FCSTD DOCUMENT  (FreeCAD 0.20R29410 (Git))
Label: parallel_port_pinout
License: All rights reserved
LicenseURL: http://en.wikipedia.org/wiki/All_rights_reserved
objects: App::FeaturePython×43, Part::Part2DObjectPython×25, Sketcher::SketchObject×1, Part::Feature×1, App::DocumentObjectGroup×1, TechDraw::DrawSVGTemplate×1, App::Part×1, TechDraw::DrawViewPart×1, TechDraw::DrawPage×1
note: 27 computed .brp shape members not serialized (recipe doc carries the construction recipe); baked Part::Feature solids carry a one-line shape summary decoded from their .brp

FEATURE [Sketcher::SketchObject] Sketch
  FullyConstrained = false
  sketch-geometry (45):
    g0: Circle CenterX=-16.62 CenterY=1.42 CenterZ=0 NormalX=0 NormalY=0 NormalZ=1 AngleXU=0 Radius=0.64
    g1: Circle CenterX=-13.85 CenterY=1.42 CenterZ=0 NormalX=0 NormalY=0 NormalZ=1 AngleXU=0 Radius=0.64
    g2: Circle CenterX=-11.08 CenterY=1.42 CenterZ=0 NormalX=0 NormalY=0 NormalZ=1 AngleXU=0 Radius=0.64
    g3: Circle CenterX=-8.31 CenterY=1.42 CenterZ=0 NormalX=0 NormalY=0 NormalZ=1 AngleXU=0 Radius=0.64
    g4: Circle CenterX=16.62 CenterY=1.42 CenterZ=0 NormalX=0 NormalY=0 NormalZ=1 AngleXU=0 Radius=0.64
    g5: LineSegment StartX=-16.62 StartY=1.42 StartZ=0 EndX=16.62 EndY=1.42 EndZ=0
    g6: Circle CenterX=-5.54 CenterY=1.42 CenterZ=0 NormalX=0 NormalY=0 NormalZ=1 AngleXU=0 Radius=0.64
    g7: Circle CenterX=-2.77 CenterY=1.42 CenterZ=0 NormalX=0 NormalY=0 NormalZ=1 AngleXU=0 Radius=0.64
    g8: Circle CenterX=-2e-16 CenterY=1.42 CenterZ=0 NormalX=0 NormalY=0 NormalZ=1 AngleXU=0 Radius=0.64
    g9: Circle CenterX=2.77 CenterY=1.42 CenterZ=0 NormalX=0 NormalY=0 NormalZ=1 AngleXU=0 Radius=0.64
    g10: Circle CenterX=5.54 CenterY=1.42 CenterZ=0 NormalX=0 NormalY=0 NormalZ=1 AngleXU=0 Radius=0.64
    g11: Circle CenterX=8.31 CenterY=1.42 CenterZ=0 NormalX=0 NormalY=0 NormalZ=1 AngleXU=0 Radius=0.64
    g12: Circle CenterX=11.08 CenterY=1.42 CenterZ=0 NormalX=0 NormalY=0 NormalZ=1 AngleXU=0 Radius=0.64
    g13: Circle CenterX=13.85 CenterY=1.42 CenterZ=0 NormalX=0 NormalY=0 NormalZ=1 AngleXU=0 Radius=0.64
    g14: LineSegment StartX=-15.235 StartY=-1.42 StartZ=0 EndX=15.235 EndY=-1.42 EndZ=0
    g15: Circle CenterX=-15.235 CenterY=-1.42 CenterZ=0 NormalX=0 NormalY=0 NormalZ=1 AngleXU=0 Radius=0.64
    g16: Circle CenterX=-12.465 CenterY=-1.42 CenterZ=0 NormalX=0 NormalY=0 NormalZ=1 AngleXU=0 Radius=0.64
    g17: Circle CenterX=-9.695 CenterY=-1.42 CenterZ=0 NormalX=0 NormalY=0 NormalZ=1 AngleXU=0 Radius=0.64
    g18: Circle CenterX=-6.925 CenterY=-1.42 CenterZ=0 NormalX=0 NormalY=0 NormalZ=1 AngleXU=0 Radius=0.64
    g19: Circle CenterX=-4.155 CenterY=-1.42 CenterZ=0 NormalX=0 NormalY=0 NormalZ=1 AngleXU=0 Radius=0.64
    g20: Circle CenterX=-1.385 CenterY=-1.42 CenterZ=0 NormalX=0 NormalY=0 NormalZ=1 AngleXU=0 Radius=0.64
    g21: Circle CenterX=1.385 CenterY=-1.42 CenterZ=0 NormalX=0 NormalY=0 NormalZ=1 AngleXU=0 Radius=0.64
    g22: Circle CenterX=4.155 CenterY=-1.42 CenterZ=0 NormalX=0 NormalY=0 NormalZ=1 AngleXU=0 Radius=0.64
    g23: Circle CenterX=6.925 CenterY=-1.42 CenterZ=0 NormalX=0 NormalY=0 NormalZ=1 AngleXU=0 Radius=0.64
    g24: Circle CenterX=9.695 CenterY=-1.42 CenterZ=0 NormalX=0 NormalY=0 NormalZ=1 AngleXU=0 Radius=0.64
    g25: Circle CenterX=12.465 CenterY=-1.42 CenterZ=0 NormalX=0 NormalY=0 NormalZ=1 AngleXU=0 Radius=0.64
    g26: Circle CenterX=15.235 CenterY=-1.42 CenterZ=0 NormalX=0 NormalY=0 NormalZ=1 AngleXU=0 Radius=0.64
    g27: GeomPoint X=-2e-16 Y=-1.42 Z=0
    g28: LineSegment StartX=-16.81 StartY=4.18 StartZ=0 EndX=16.81 EndY=4.18 EndZ=0
    g29: LineSegment StartX=-16.2775 StartY=-4.18 StartZ=0 EndX=16.2775 EndY=-4.18 EndZ=0
    g30: LineSegment StartX=19.4394 StartY=1.04636 StartZ=0 EndX=18.9069 EndY=-1.97364 EndZ=0
    g31: LineSegment StartX=-19.4394 StartY=1.04636 StartZ=0 EndX=-18.9069 EndY=-1.97364 EndZ=0
    g32: ArcOfCircle CenterX=-16.81 CenterY=1.51 CenterZ=0 NormalX=0 NormalY=0 NormalZ=1 AngleXU=0 Radius=2.67 StartAngle=1.5708 EndAngle=3.31613
    g33: ArcOfCircle CenterX=-16.2775 CenterY=-1.51 CenterZ=0 NormalX=0 NormalY=0 NormalZ=1 AngleXU=0 Radius=2.67 StartAngle=3.31613 EndAngle=4.71239
    g34: ArcOfCircle CenterX=16.81 CenterY=1.51 CenterZ=0 NormalX=0 NormalY=0 NormalZ=1 AngleXU=0 Radius=2.67 StartAngle=6.10865 EndAngle=7.85398
    g35: ArcOfCircle CenterX=16.2775 CenterY=-1.51 CenterZ=0 NormalX=0 NormalY=0 NormalZ=1 AngleXU=0 Radius=2.67 StartAngle=4.71239 EndAngle=6.10865
    g36: LineSegment StartX=19.4394 StartY=1.04636 StartZ=0 EndX=19.4394 EndY=-2.3777 EndZ=0
    g37: LineSegment StartX=-19.4394 StartY=1.04636 StartZ=0 EndX=-19.4394 EndY=-0.673424 EndZ=0
    g38: LineSegment StartX=-16.81 StartY=1.51 StartZ=0 EndX=16.81 EndY=1.51 EndZ=0
    g39: LineSegment StartX=-16.2775 StartY=-1.51 StartZ=0 EndX=16.2775 EndY=-1.51 EndZ=0
    g40: LineSegment StartX=-19.48 StartY=3.07637 StartZ=0 EndX=-19.48 EndY=-2.31562 EndZ=0
    g41: GeomPoint X=-19.48 Y=1.50999 Z=0
    g42: LineSegment StartX=16.81 StartY=1.51 StartZ=0 EndX=19.48 EndY=1.51 EndZ=0
    g43: GeomPoint X=0 Y=4.18 Z=0
    g44: GeomPoint X=0 Y=-4.18 Z=0
  constraints (114):
    c: Coincident(g5,g0)
    c: Coincident(g5,g4)
    c: PointOnObject(g3,g5)
    c: PointOnObject(g2,g5)
    c: PointOnObject(g1,g5)
    c: PointOnObject(g6,g5)
    c: PointOnObject(g7,g5)
    c: PointOnObject(g8,g5)
    c: PointOnObject(g9,g5)
    c: PointOnObject(g10,g5)
    c: PointOnObject(g11,g5)
    c: PointOnObject(g12,g5)
    c: PointOnObject(g13,g5)
    c: Equal(g3,g2)
    c: Equal(g2,g1)
    c: Equal(g1,g0)
    c: Equal(g0,g6)
    c: Equal(g6,g7)
    c: Equal(g7,g8)
    c: Equal(g8,g9)
    c: Equal(g9,g10)
    c: Equal(g10,g11)
    c: Equal(g11,g12)
    c: Equal(g12,g13)
    c: Equal(g13,g4)
    c: Radius(g0) = 0.64
    c: DistanceX(g0,g1) = 2.77
    c: DistanceX(g1,g2) = 2.77
    c: DistanceX(g2,g3) = 2.77
    c: DistanceX(g3,g6) = 2.77
    c: DistanceX(g6,g7) = 2.77
    c: DistanceX(g7,g8) = 2.77
    c: DistanceX(g8,g9) = 2.77
    c: DistanceX(g9,g10) = 2.77
    c: DistanceX(g10,g11) = 2.77
    c: DistanceX(g11,g12) = 2.77
    c: DistanceX(g12,g13) = 2.77
    c: DistanceX(g13,g4) = 2.77
    c: Symmetric(g0,g4,g-2)
    c: Symmetric(g14,g14,g-2)
    c: Coincident(g15,g14)
    c: PointOnObject(g16,g14)
    c: PointOnObject(g17,g14)
    c: PointOnObject(g18,g14)
    c: PointOnObject(g19,g14)
    c: PointOnObject(g20,g14)
    c: PointOnObject(g21,g14)
    c: PointOnObject(g22,g14)
    c: PointOnObject(g23,g14)
    c: PointOnObject(g24,g14)
    c: PointOnObject(g25,g14)
    c: Coincident(g26,g14)
    c: Equal(g15,g16)
    c: Equal(g16,g17)
    c: Equal(g17,g18)
    c: Equal(g18,g19)
    c: Equal(g19,g20)
    c: Equal(g20,g21)
    c: Equal(g21,g22)
    c: Equal(g22,g23)
    c: Equal(g23,g24)
    c: Equal(g24,g25)
    c: Equal(g25,g26)
    c: Equal(g26,g0)
    c: DistanceX(g14,g16) = 2.77
    c: DistanceX(g16,g17) = 2.77
    c: DistanceX(g17,g18) = 2.77
    c: DistanceX(g18,g19) = 2.77
    c: DistanceX(g19,g20) = 2.77
    c: DistanceX(g20,g21) = 2.77
    c: DistanceX(g21,g22) = 2.77
    c: DistanceX(g22,g23) = 2.77
    c: DistanceX(g23,g24) = 2.77
    c: DistanceX(g24,g25) = 2.77
    c: DistanceX(g25,g14) = 2.77
    c: DistanceY(g15,g0) = 2.84
    c: PointOnObject(g27,g14)
    c: Symmetric(g27,g8,g-1)
    c: Tangent(g32,g31) = -1.5708
    c: Tangent(g28,g32) = 1.5708
    c: Tangent(g33,g31) = -1.5708
    c: Tangent(g33,g29) = -1.5708
    c: Tangent(g34,g28) = 1.5708
    c: Tangent(g34,g30) = 1.5708
    c: Tangent(g35,g29) = -1.5708
    c: Tangent(g35,g30) = 1.5708
    c: Coincident(g36,g30)
    c: Vertical(g36)
    c: Angle(g30,g36) = 0.174533
    c: Coincident(g37,g31)
    c: Vertical(g37)
    c: Angle(g37,g31) = 0.174533
    c: DistanceY(g29,g28) = 8.36
    c: Symmetric(g28,g28,g-2)
    c: Symmetric(g29,g29,g-2)
    c: Coincident(g38,g32)
    c: Coincident(g38,g34)
    c: Horizontal(g38)
    c: Coincident(g39,g33)
    c: Coincident(g39,g35)
    c: Vertical(g40)
    c: Tangent(g40,g32)
    c: PointOnObject(g41,g32)
    c: PointOnObject(g41,g40)
    c: Coincident(g42,g34)
    c: Horizontal(g42)
    c: PointOnObject(g42,g34)
    c: DistanceX(g41,g42) = 38.96
    c: PointOnObject(g43,g-2)
    c: PointOnObject(g43,g28)
    c: PointOnObject(g44,g29)
    c: Symmetric(g44,g43,g-1)
    c: Radius(g32) = 2.67
    c: Equal(g33,g32)
FEATURE [Part::Part2DObjectPython] Circle  # Draft 2D object (typed FeaturePython)
  Area = 1.2868
  FirstAngle = 0
  LastAngle = 0
  MakeFace = true
  Placement = pos=(-16.62,1.42,0) rot=(0,0,1;0rad)
  Radius = 0.64
FEATURE [Part::Part2DObjectPython] Circle001  # Draft 2D object (typed FeaturePython)
  Area = 1.2868
  FirstAngle = 0
  LastAngle = 0
  MakeFace = true
  Placement = pos=(-13.85,1.42,0) rot=(0,0,1;0rad)
  Radius = 0.64
FEATURE [Part::Part2DObjectPython] Circle002  # Draft 2D object (typed FeaturePython)
  Area = 1.2868
  FirstAngle = 0
  LastAngle = 0
  MakeFace = true
  Placement = pos=(-11.08,1.42,0) rot=(0,0,1;0rad)
  Radius = 0.64
FEATURE [Part::Part2DObjectPython] Circle003  # Draft 2D object (typed FeaturePython)
  Area = 1.2868
  FirstAngle = 0
  LastAngle = 0
  MakeFace = true
  Placement = pos=(-8.31,1.42,0) rot=(0,0,1;0rad)
  Radius = 0.64
FEATURE [Part::Part2DObjectPython] Circle004  # Draft 2D object (typed FeaturePython)
  Area = 1.2868
  FirstAngle = 0
  LastAngle = 0
  MakeFace = true
  Placement = pos=(16.62,1.42,0) rot=(0,0,1;0rad)
  Radius = 0.64
FEATURE [Part::Part2DObjectPython] Circle005  # Draft 2D object (typed FeaturePython)
  Area = 1.2868
  FirstAngle = 0
  LastAngle = 0
  MakeFace = true
  Placement = pos=(-5.54,1.42,0) rot=(0,0,1;0rad)
  Radius = 0.64
FEATURE [Part::Part2DObjectPython] Circle006  # Draft 2D object (typed FeaturePython)
  Area = 1.2868
  FirstAngle = 0
  LastAngle = 0
  MakeFace = true
  Placement = pos=(-2.77,1.42,0) rot=(0,0,1;0rad)
  Radius = 0.64
FEATURE [Part::Part2DObjectPython] Circle007  # Draft 2D object (typed FeaturePython)
  Area = 1.2868
  FirstAngle = 0
  LastAngle = 0
  MakeFace = true
  Placement = pos=(-2e-16,1.42,0) rot=(0,0,1;0rad)
  Radius = 0.64
FEATURE [Part::Part2DObjectPython] Circle008  # Draft 2D object (typed FeaturePython)
  Area = 1.2868
  FirstAngle = 0
  LastAngle = 0
  MakeFace = true
  Placement = pos=(2.77,1.42,0) rot=(0,0,1;0rad)
  Radius = 0.64
FEATURE [Part::Part2DObjectPython] Circle009  # Draft 2D object (typed FeaturePython)
  Area = 1.2868
  FirstAngle = 0
  LastAngle = 0
  MakeFace = true
  Placement = pos=(5.54,1.42,0) rot=(0,0,1;0rad)
  Radius = 0.64
FEATURE [Part::Part2DObjectPython] Circle010  # Draft 2D object (typed FeaturePython)
  Area = 1.2868
  FirstAngle = 0
  LastAngle = 0
  MakeFace = true
  Placement = pos=(8.31,1.42,0) rot=(0,0,1;0rad)
  Radius = 0.64
FEATURE [Part::Part2DObjectPython] Circle011  # Draft 2D object (typed FeaturePython)
  Area = 1.2868
  FirstAngle = 0
  LastAngle = 0
  MakeFace = true
  Placement = pos=(11.08,1.42,0) rot=(0,0,1;0rad)
  Radius = 0.64
FEATURE [Part::Part2DObjectPython] Circle012  # Draft 2D object (typed FeaturePython)
  Area = 1.2868
  FirstAngle = 0
  LastAngle = 0
  MakeFace = true
  Placement = pos=(13.85,1.42,0) rot=(0,0,1;0rad)
  Radius = 0.64
FEATURE [Part::Part2DObjectPython] Circle013  # Draft 2D object (typed FeaturePython)
  Area = 1.2868
  FirstAngle = 0
  LastAngle = 0
  MakeFace = true
  Placement = pos=(-15.235,-1.42,0) rot=(0,0,1;0rad)
  Radius = 0.64
FEATURE [Part::Part2DObjectPython] Circle014  # Draft 2D object (typed FeaturePython)
  Area = 1.2868
  FirstAngle = 0
  LastAngle = 0
  MakeFace = true
  Placement = pos=(-12.465,-1.42,0) rot=(0,0,1;0rad)
  Radius = 0.64
FEATURE [Part::Part2DObjectPython] Circle015  # Draft 2D object (typed FeaturePython)
  Area = 1.2868
  FirstAngle = 0
  LastAngle = 0
  MakeFace = true
  Placement = pos=(-9.695,-1.42,0) rot=(0,0,1;0rad)
  Radius = 0.64
FEATURE [Part::Part2DObjectPython] Circle016  # Draft 2D object (typed FeaturePython)
  Area = 1.2868
  FirstAngle = 0
  LastAngle = 0
  MakeFace = true
  Placement = pos=(-6.925,-1.42,0) rot=(0,0,1;0rad)
  Radius = 0.64
FEATURE [Part::Part2DObjectPython] Circle017  # Draft 2D object (typed FeaturePython)
  Area = 1.2868
  FirstAngle = 0
  LastAngle = 0
  MakeFace = true
  Placement = pos=(-4.155,-1.42,0) rot=(0,0,1;0rad)
  Radius = 0.64
FEATURE [Part::Part2DObjectPython] Circle018  # Draft 2D object (typed FeaturePython)
  Area = 1.2868
  FirstAngle = 0
  LastAngle = 0
  MakeFace = true
  Placement = pos=(-1.385,-1.42,0) rot=(0,0,1;0rad)
  Radius = 0.64
FEATURE [Part::Part2DObjectPython] Circle019  # Draft 2D object (typed FeaturePython)
  Area = 1.2868
  FirstAngle = 0
  LastAngle = 0
  MakeFace = true
  Placement = pos=(1.385,-1.42,0) rot=(0,0,1;0rad)
  Radius = 0.64
FEATURE [Part::Part2DObjectPython] Circle020  # Draft 2D object (typed FeaturePython)
  Area = 1.2868
  FirstAngle = 0
  LastAngle = 0
  MakeFace = true
  Placement = pos=(4.155,-1.42,0) rot=(0,0,1;0rad)
  Radius = 0.64
FEATURE [Part::Part2DObjectPython] Circle021  # Draft 2D object (typed FeaturePython)
  Area = 1.2868
  FirstAngle = 0
  LastAngle = 0
  MakeFace = true
  Placement = pos=(6.925,-1.42,0) rot=(0,0,1;0rad)
  Radius = 0.64
FEATURE [Part::Part2DObjectPython] Circle022  # Draft 2D object (typed FeaturePython)
  Area = 1.2868
  FirstAngle = 0
  LastAngle = 0
  MakeFace = true
  Placement = pos=(9.695,-1.42,0) rot=(0,0,1;0rad)
  Radius = 0.64
FEATURE [Part::Part2DObjectPython] Circle023  # Draft 2D object (typed FeaturePython)
  Area = 1.2868
  FirstAngle = 0
  LastAngle = 0
  MakeFace = true
  Placement = pos=(12.465,-1.42,0) rot=(0,0,1;0rad)
  Radius = 0.64
FEATURE [Part::Part2DObjectPython] Circle024  # Draft 2D object (typed FeaturePython)
  Area = 1.2868
  FirstAngle = 0
  LastAngle = 0
  MakeFace = true
  Placement = pos=(15.235,-1.42,0) rot=(0,0,1;0rad)
  Radius = 0.64
FEATURE [Part::Feature] Sketch001
  shape: bbox 38.96 x 8.36 x 2e-07 mm, 0 faces, 0 solids (baked)
FEATURE [App::FeaturePython] Text  # WARN: FeaturePython — macro-defined, semantics opaque (R4)
  Placement = pos=(16.3199,1.1133,-1e-16) rot=(0,0,1;0rad)
  Text = 1
FEATURE [App::DocumentObjectGroup] Group
FEATURE [App::FeaturePython] Text001  # WARN: FeaturePython — macro-defined, semantics opaque (R4)
  Placement = pos=(13.5545,1.11266,0) rot=(0,0,1;0rad)
  Text = 2
FEATURE [App::FeaturePython] Text002  # WARN: FeaturePython — macro-defined, semantics opaque (R4)
  Placement = pos=(10.7908,1.05727,0) rot=(0,0,1;0rad)
  Text = 3
FEATURE [App::FeaturePython] Text003  # WARN: FeaturePython — macro-defined, semantics opaque (R4)
  Placement = pos=(7.98701,1.09636,0) rot=(0,0,1;0rad)
  Text = 4
FEATURE [App::FeaturePython] Text004  # WARN: FeaturePython — macro-defined, semantics opaque (R4)
  Placement = pos=(5.24921,1.07724,0) rot=(0,0,1;0rad)
  Text = 5
FEATURE [App::FeaturePython] Text005  # WARN: FeaturePython — macro-defined, semantics opaque (R4)
  Placement = pos=(2.45988,1.10687,0) rot=(0,0,1;0rad)
  Text = 6
FEATURE [App::FeaturePython] Text006  # WARN: FeaturePython — macro-defined, semantics opaque (R4)
  Placement = pos=(-0.275752,1.06897,0) rot=(0,0,1;0rad)
  Text = 7
FEATURE [App::FeaturePython] Text007  # WARN: FeaturePython — macro-defined, semantics opaque (R4)
  Placement = pos=(-3.06267,1.07824,0) rot=(0,0,1;0rad)
  Text = 8
FEATURE [App::FeaturePython] Text008  # WARN: FeaturePython — macro-defined, semantics opaque (R4)
  Placement = pos=(-5.82214,1.08719,0) rot=(0,0,1;0rad)
  Text = 9
FEATURE [App::FeaturePython] Text009  # WARN: FeaturePython — macro-defined, semantics opaque (R4)
  Placement = pos=(-15.7989,-1.73226,0) rot=(0,0,1;0rad)
  Text = 25
FEATURE [App::FeaturePython] Text010  # WARN: FeaturePython — macro-defined, semantics opaque (R4)
  Placement = pos=(-8.88111,1.08351,0) rot=(0,0,1;0rad)
  Text = 10
FEATURE [App::FeaturePython] Text011  # WARN: FeaturePython — macro-defined, semantics opaque (R4)
  Placement = pos=(-11.6819,1.07691,0) rot=(0,0,1;0rad)
  Text = 11
FEATURE [App::FeaturePython] Text012  # WARN: FeaturePython — macro-defined, semantics opaque (R4)
  Placement = pos=(-14.4308,1.0661,0) rot=(0,0,1;0rad)
  Text = 12
FEATURE [App::FeaturePython] Text013  # WARN: FeaturePython — macro-defined, semantics opaque (R4)
  Placement = pos=(-17.1901,1.07831,0) rot=(0,0,1;0rad)
  Text = 13
FEATURE [App::FeaturePython] Text014  # WARN: FeaturePython — macro-defined, semantics opaque (R4)
  Placement = pos=(14.6575,-1.79361,0) rot=(0,0,1;0rad)
  Text = 14
FEATURE [App::FeaturePython] Text015  # WARN: FeaturePython — macro-defined, semantics opaque (R4)
  Placement = pos=(11.9056,-1.77541,0) rot=(0,0,1;0rad)
  Text = 15
FEATURE [App::FeaturePython] Text016  # WARN: FeaturePython — macro-defined, semantics opaque (R4)
  Placement = pos=(9.12473,-1.76791,0) rot=(0,0,1;0rad)
  Text = 16
FEATURE [App::FeaturePython] Text017  # WARN: FeaturePython — macro-defined, semantics opaque (R4)
  Placement = pos=(6.31445,-1.77817,0) rot=(0,0,1;0rad)
  Text = 17
FEATURE [App::FeaturePython] Text018  # WARN: FeaturePython — macro-defined, semantics opaque (R4)
  Placement = pos=(3.57708,-1.78271,0) rot=(0,0,1;0rad)
  Text = 18
FEATURE [App::FeaturePython] Text019  # WARN: FeaturePython — macro-defined, semantics opaque (R4)
  Placement = pos=(0.796046,-1.76558,0) rot=(0,0,1;0rad)
  Text = 19
FEATURE [App::FeaturePython] Text020  # WARN: FeaturePython — macro-defined, semantics opaque (R4)
  Placement = pos=(-1.94609,-1.7508,0) rot=(0,0,1;0rad)
  Text = 20
FEATURE [App::FeaturePython] Text021  # WARN: FeaturePython — macro-defined, semantics opaque (R4)
  Placement = pos=(-4.70275,-1.77229,0) rot=(0,0,1;0rad)
  Text = 21
FEATURE [App::FeaturePython] Text022  # WARN: FeaturePython — macro-defined, semantics opaque (R4)
  Placement = pos=(-7.50552,-1.73882,0) rot=(0,0,1;0rad)
  Text = 22
FEATURE [App::FeaturePython] Text023  # WARN: FeaturePython — macro-defined, semantics opaque (R4)
  Placement = pos=(-10.2783,-1.75871,0) rot=(0,0,1;0rad)
  Text = 23
FEATURE [App::FeaturePython] Text024  # WARN: FeaturePython — macro-defined, semantics opaque (R4)
  Placement = pos=(-13.0295,-1.77128,0) rot=(0,0,1;0rad)
  Text = 24
FEATURE [App::FeaturePython] Text025  # WARN: FeaturePython — macro-defined, semantics opaque (R4)
  Placement = pos=(16.62,1.42,0) rot=(0,0,1;0.785398rad)
  Text =    nSTROBE
FEATURE [App::FeaturePython] Text026  # WARN: FeaturePython — macro-defined, semantics opaque (R4)
  Placement = pos=(13.85,1.42,0) rot=(0,0,1;0.785398rad)
  Text =     D0
FEATURE [App::FeaturePython] Text027  # WARN: FeaturePython — macro-defined, semantics opaque (R4)
  Placement = pos=(11.08,1.42,0) rot=(0,0,1;0.785398rad)
  Text =    D1
FEATURE [App::FeaturePython] Text028  # WARN: FeaturePython — macro-defined, semantics opaque (R4)
  Placement = pos=(8.31,1.42,0) rot=(0,0,1;0.785398rad)
  Text =    D2
FEATURE [App::FeaturePython] Text029  # WARN: FeaturePython — macro-defined, semantics opaque (R4)
  Placement = pos=(5.54,1.42,0) rot=(0,0,1;0.785398rad)
  Text =    D3
FEATURE [App::FeaturePython] Text030  # WARN: FeaturePython — macro-defined, semantics opaque (R4)
  Placement = pos=(2.77,1.42,0) rot=(0,0,1;0.785398rad)
  Text =    D4
FEATURE [App::FeaturePython] Text031  # WARN: FeaturePython — macro-defined, semantics opaque (R4)
  Placement = pos=(0,1.42,0) rot=(0,0,1;0.785398rad)
  Text =    D5
FEATURE [App::FeaturePython] Text032  # WARN: FeaturePython — macro-defined, semantics opaque (R4)
  Placement = pos=(-2.77,1.42,0) rot=(0,0,1;0.785398rad)
  Text =    D6
FEATURE [App::FeaturePython] Text033  # WARN: FeaturePython — macro-defined, semantics opaque (R4)
  Placement = pos=(-5.54,1.42,0) rot=(0,0,1;0.785398rad)
  Text =    D7
FEATURE [App::FeaturePython] Text034  # WARN: FeaturePython — macro-defined, semantics opaque (R4)
  Placement = pos=(-8.31,1.42,0) rot=(0,0,1;0.785398rad)
  Text =    nACK
FEATURE [App::FeaturePython] Text035  # WARN: FeaturePython — macro-defined, semantics opaque (R4)
  Placement = pos=(-11.08,1.42,0) rot=(0,0,1;0.785398rad)
  Text =    BUSY
FEATURE [App::FeaturePython] Text036  # WARN: FeaturePython — macro-defined, semantics opaque (R4)
  Placement = pos=(-13.85,1.42,0) rot=(0,0,1;0.785398rad)
  Text =    PE
FEATURE [App::FeaturePython] Text037  # WARN: FeaturePython — macro-defined, semantics opaque (R4)
  Placement = pos=(-16.62,1.42,0) rot=(0,0,1;0.785398rad)
  Text =    SEL
FEATURE [App::FeaturePython] Text038  # WARN: FeaturePython — macro-defined, semantics opaque (R4)
  Placement = pos=(15.23,-1.42,0) rot=(0,0,1;-0.785398rad)
  Text =    nAUTOF
FEATURE [App::FeaturePython] Text039  # WARN: FeaturePython — macro-defined, semantics opaque (R4)
  Placement = pos=(12.46,-1.42,0) rot=(0,0,1;-0.785398rad)
  Text =    nERROR
FEATURE [App::FeaturePython] Text040  # WARN: FeaturePython — macro-defined, semantics opaque (R4)
  Placement = pos=(9.7,-1.42,0) rot=(0,0,1;-0.785398rad)
  Text =    nINIT
FEATURE [App::FeaturePython] Text041  # WARN: FeaturePython — macro-defined, semantics opaque (R4)
  Placement = pos=(6.92,-1.42,0) rot=(0,0,1;-0.785398rad)
  Text =    nSELIN
FEATURE [App::FeaturePython] Text042  # WARN: FeaturePython — macro-defined, semantics opaque (R4)
  Placement = pos=(-3.79714,-3.56261,0) rot=(0,0,1;0rad)
  Text = GND
FEATURE [TechDraw::DrawSVGTemplate] Template
  Height = 210
  Orientation = 1
  Width = 297
FEATURE [App::Part] Part
  Group = -> [Sketch001,Circle024,Circle023,Circle022,Circle021,Circle019,Circle017,Circle016,Circle015,Circle014,Circle013,Circle005,Circle010,Circle001,Circle002,Circle009,Circle003,Circle011,Circle004,Circle020,Circle006,Circle012,Circle007,Circle018,Circle,Circle008,Text001,Text002,Text003,Text004,Text005,Text006,Text007,Text008,Text009,Text010,Text011,Text012,Text013,Text014,Text015,Text016,Text017,+26 more]
  Origin = -> Origin
FEATURE [TechDraw::DrawViewPart] View
  CoarseView = false
  Direction = (0,0,1)
  Focus = 100
  HardHidden = false
  IsoCount = 0
  IsoHidden = false
  IsoVisible = false
  LockPosition = false
  Perspective = false
  Rotation = 0
  ScaleType = 0
  SeamHidden = false
  SeamVisible = true
  SmoothHidden = false
  SmoothVisible = true
  Source = -> [Template]
  X = 138.503
  XDirection = (1,0,0)
  Y = 112.695
FEATURE [TechDraw::DrawPage] Page
  KeepUpdated = true
  NextBalloonIndex = 1
  ProjectionType = 0
  Template = -> Template
  Views = -> [View]
